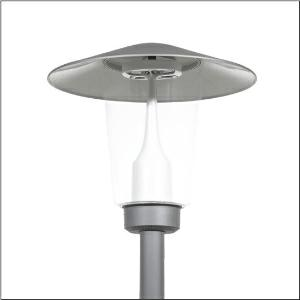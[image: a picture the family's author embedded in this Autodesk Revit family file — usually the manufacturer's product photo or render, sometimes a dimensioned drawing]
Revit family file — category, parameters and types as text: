
# Revit family: pilzleuchte_iq___st1_2a_5xa5235mf14h_7035
name_source: partatom
category: Lighting Fixtures
units: mm (PartAtom-declared; Revit-internal decimal feet)

## family parameters
Cut with Voids When Loaded = No
Host = Face
Light Source = No
Part Type = Normal
Room Calculation Point = No
Round Connector Dimension = Use Diameter
Shared = No

## types (1)
- --- (1 x LED, 1550 lm, 11.8 W, 2700K)
    Apparent Load = 12 VA
    CIE Flux Codes = 24 61 93 98 100
    Color Rendering = 70
    Color Temperature = 2700K
    Default Elevation = 1800 mm
    Description = Mushroom Luminaire iQ, mast luminaire, Module 540 iQ-SR, primary light control with 3 zone facetted reflector, of plastic, silver coated, highly specular, structured, primary optical cover: cover, of PMMA, transparent, light distribution: ST1.2a, light emission: direct distribution, primary light characteristic: asymmetric, installation type: post-top, LED, High Power LED, rated luminous flux: 1.550lm, luminous efficacy: 131lm/W, light colour: 727, colour temperature: 2700K, control gear: ECG iQ, control: presetting dimming logarithmic, Street-Remote, Auto-Match, Temp-Guard, Lumen-Switch, Night-Set, Smart-Wire, Light-Fading, Desk-Remote (wireless, voltage-free reading and setting of iQ features in the workshop via application-optimized NFC function/RFID function), optimised constant luminous flux control (CLO 2.0), with terminal, 6-pole, max. 2.5mm², mains connection: 230..240V, AC, 50/60Hz, start of lifetime: 12W, end of service life: 12W, reduction: 6W, luminaire housing, upper part, of glass-fibre reinforced polyester, coated, Siteco® metallic grey (DB 702S), diameter: 650mm, height: 586mm, spigot size: d x l = 76 x 70mm (post-top) | with reducer (optional accessory) 60 x 70mm, post-top mast mounting element, of diecast aluminium, coated, Siteco® metallic grey (DB 702S), Module 540 iQ-SR, traffic white (RAL 9016), equipment: standard, protection rating (complete): IP65, insulation class (complete): insulation class II (safety insulation), certification: CE, ENEC, VDE, packaging unit: 1 piece

Light Distribution: ST1.2a
    Height = 586 mm
    Lamp = 1 x LED
    Lamp Light Flux = 1550 lm
    Lamp Power = 11.8 W
    Lamp count = 1
    Length = 650 mm
    Luminous efficacy = 131 lm/W
    Manufacturer = Siteco
    ModVariant = No
    Model = 5XA5235MF14H
    Number of Poles = 1
    OnlyDefault = Yes
    Power Factor = 1
    Product Name = Pilzleuchte iQ | ST1.2a
    Product group = mast luminaire | pylon top
    ProductGroupID = 6100
    Protection Class = Protection class II
    Protection Degree = IP 65
    RLX_Detail_Level = 1
    RLX_Emergency_Light_Flux = 0 lm
    RLX_Emergency_Type = 0
    RLX_Emergency_Type_DB = No
    RlxData = <blob elided: 123277 chars, md5=66a42d3f>
    Socket = socket
    Standby Power = 0 W
    System Light Flux = 1550 lm
    System Power = 12 W
    Type Comments = factory setting: luminous flux: 100 % | dim-lin: 254 | 472 mA
    Type Image = l_1006077.jpg
    URL = http://relux.com
    VarID = @adj_103595
    Voltage = 0 V
    Weight = 0.00 kg
    Width = 0 mm  [stored 0 ft]

note: [stored X ft] marks values corroborated as IEEE doubles in the binary element streams (Revit-internal decimal feet)

## geometry (parser evidence)
native form markers: Blend x4, Sweep x11
no freeform markers — native parametric forms only
